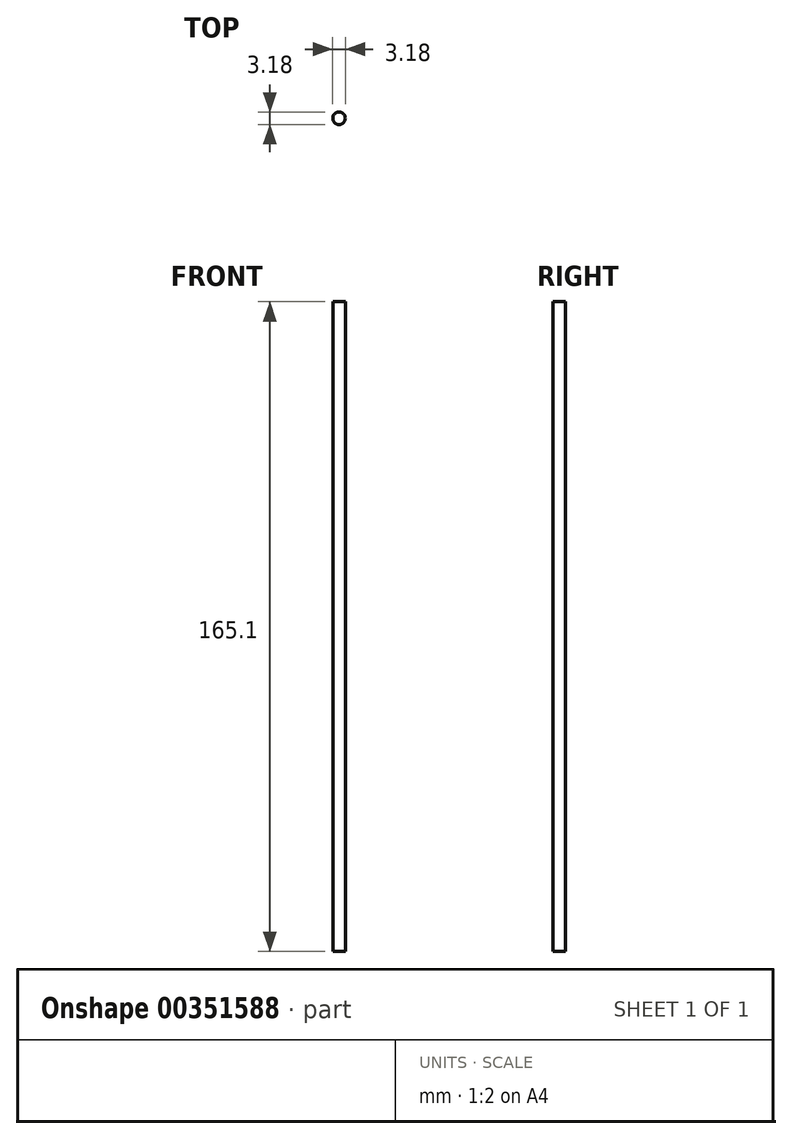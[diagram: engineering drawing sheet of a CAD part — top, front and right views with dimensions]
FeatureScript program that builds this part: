
annotation { "Feature Type Name" : "Feature", "Feature Type Description" : "" }
export const myFeature = defineFeature(function(context is Context, id is Id, definition is map)
    precondition{}
    {
        {
            var Q0;
            Q0=qCreatedBy(makeId("Top.planeOp"),FACE);
            var sketch = newSketch(context, id + "F0", { "sketchPlane" : qUnion([Q0])});
            skCircle(sketch, "E0", {"center": v(0, 0) * mm, "radius": 1.59 * mm});
            skSolve(sketch);
        }
        {
            var Q0;
            Q0 = qSketchRegion(id + "F0", true);
            extrude(context, id + "F1", {"entities" : qUnion([Q0]), "depth" : 165.1 * mm});
        }
    });
